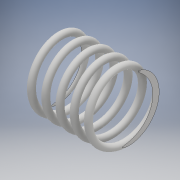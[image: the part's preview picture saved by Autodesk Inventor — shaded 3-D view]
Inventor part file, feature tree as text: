
AUTODESK INVENTOR PART (.ipt)
format: ipt  version: 2018 (Build 220112000, 112)  size: 313,856 bytes
history: native  units: mm
features: sketch x2, helix x1, extrude x1
ambient origin geometry x8: Origin, YZ Plane, XZ Plane, XY Plane, X Axis, Y Axis, Z Axis, Center Point
bodies: Solid1 (feature_tree)
feature tree (4):
  helix  "Coil1"  [1 undecoded]
  extrude  "Extrusion1"  Depth=8.9mm
  sketch  "Sketch1"  dims[d1=3.8mm]
  sketch  "Sketch2"  dims[d2=1.78mm d3=10.0mm d4=90.0mm d5=0.0mm d6=90.0deg d7=90.0deg d8=0.0mm d9=0.0mm d10=8.9mm d11=7.0mm d12=11.0mm d13=39.5mm d14=0.0mm]
note: 1 required parameter value undecoded (feature->parameter linkage not recoverable at this tier; creation-order binding heuristic only, values carry confidence <= 0.55)
